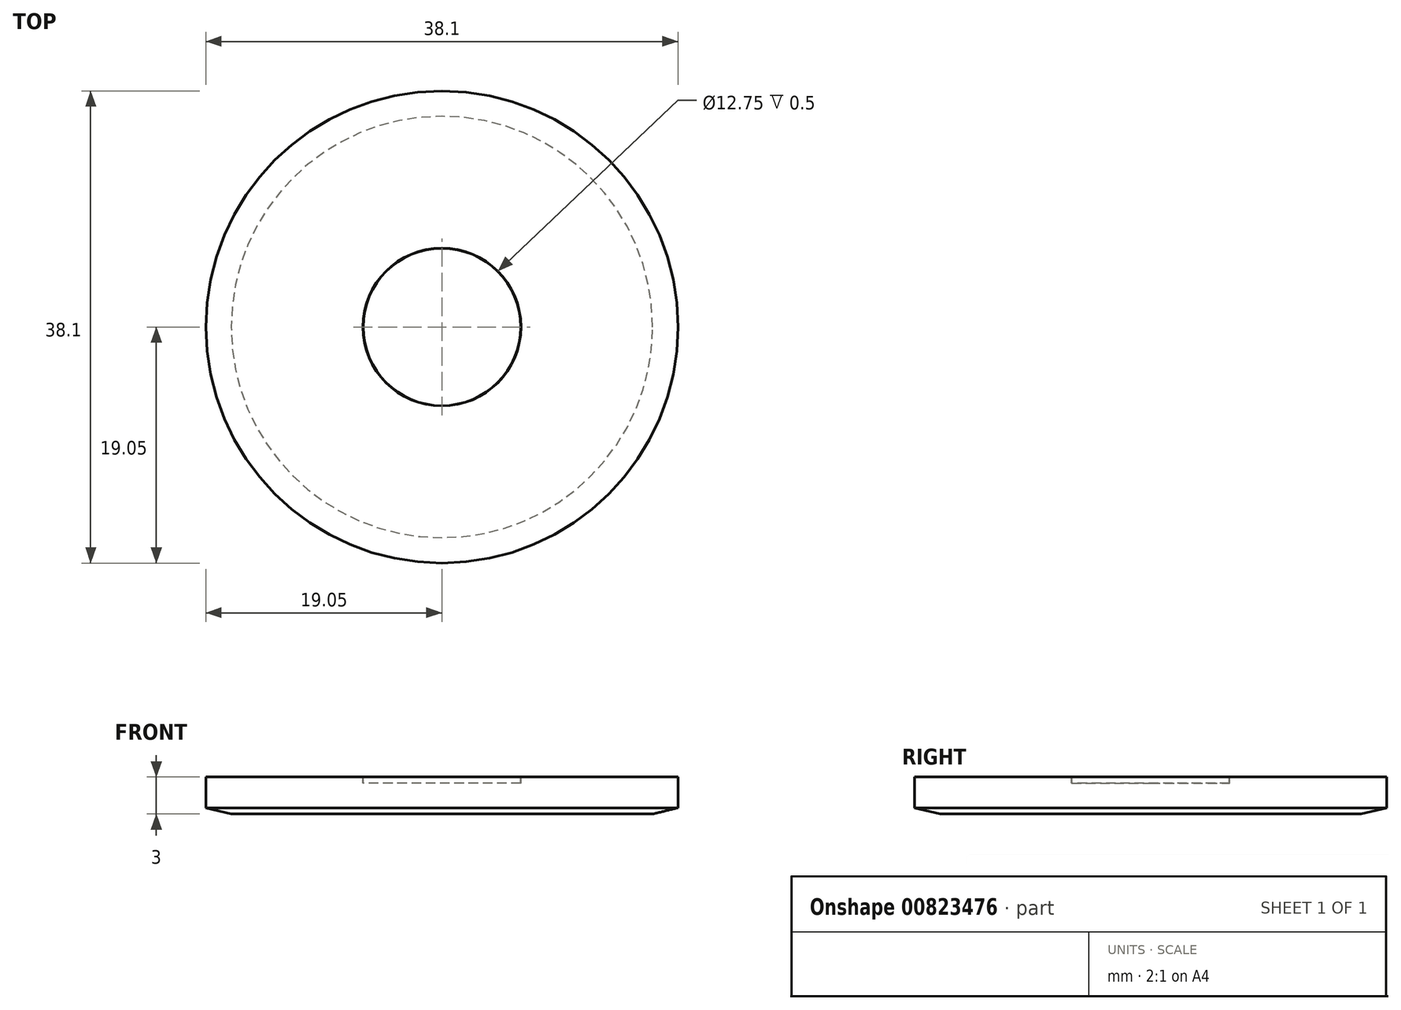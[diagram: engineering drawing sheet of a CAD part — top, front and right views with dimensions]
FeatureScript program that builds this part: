
annotation { "Feature Type Name" : "Feature", "Feature Type Description" : "" }
export const myFeature = defineFeature(function(context is Context, id is Id, definition is map)
    precondition{}
    {
        {
            var Q0;
            Q0=qCreatedBy(makeId("Top.planeOp"),FACE);
            var sketch = newSketch(context, id + "F0", { "sketchPlane" : qUnion([Q0])});
            skCircle(sketch, "E0", {"center": v(0, 0) * mm, "radius": 19.05 * mm});
            skSolve(sketch);
        }
        {
            var Q0;
            Q0=makeQuery(id+"F0.imprint","IMPRINT",FACE,{"disambiguationData":[TD([[makeQuery(id+"F0.imprint","IMPRINT",EDGE,{"derivedFrom":sQuery(id+"F0.wireOp",EDGE,"E0")}),1.0]])]});
            extrude(context, id + "F1", {"entities" : qUnion([Q0]), "depth" : 2.5 * mm, "offsetDistance" : 25 * mm});
        }
        {
            var Q0;
            Q0=makeQuery(id+"F1.opExtrude","CAP_FACE",FACE,{"disambiguationData":[OSD([sQuery(id+"F0.wireOp",EDGE,"E0")])],"isStart":false});
            var sketch = newSketch(context, id + "F2", { "sketchPlane" : qUnion([Q0])});
            skCircle(sketch, "E1", {"center": v(0, 0) * mm, "radius": 6.35 * mm});
            skCircle(sketch, "E2", {"center": v(0, 0) * mm, "radius": 6.38 * mm});
            skSolve(sketch);
        }
        {
            var Q0;
            Q0=makeQuery(id+"F2.imprint","IMPRINT",FACE,{"disambiguationData":[TD([[makeQuery(id+"F2.imprint","IMPRINT",EDGE,{"derivedFrom":sQuery(id+"F2.wireOp",EDGE,"E1")}),-1.0]])]});
            extrude(context, id + "F3", {"entities" : qUnion([Q0]), "operationType" : NewBodyOperationType.REMOVE, "oppositeDirection" : true, "depth" : .5 * mm, "offsetDistance" : 25 * mm});
        }
        {
            var Q0;
            Q0=qCreatedBy(makeId("Front.planeOp"),FACE);
            var sketch = newSketch(context, id + "F4", { "sketchPlane" : qUnion([Q0])});
            skLineSegment(sketch, "E3.0", {"start": v(-14.66, -3.4) * mm, "end": v(-8.3, -3.4) * mm});
            skArc(sketch, "E4", {"start": v(-14.66, -3.4) * mm, "mid": v(-13.73, -3.53) * mm, "end": v(-12.8, -3.65) * mm});
            skLineSegment(sketch, "E5", {"start": v(-12.8, -3.65) * mm, "end": v(-8.3, -3.65) * mm});
            skLineSegment(sketch, "E6", {"start": v(-8.3, -3.4) * mm, "end": v(-8.3, -3.65) * mm});
            skArc(sketch, "E7", {"start": v(1.27, -6.82) * mm, "mid": v(2.2, -6.95) * mm, "end": v(3.13, -7.07) * mm});
            skLineSegment(sketch, "E8", {"start": v(3.13, -7.07) * mm, "end": v(7.62, -7.07) * mm});
            skLineSegment(sketch, "E9", {"start": v(7.62, -6.82) * mm, "end": v(7.62, -7.07) * mm});
            skLineSegment(sketch, "E10", {"start": v(0, 0) * mm, "end": v(0, -0.5) * mm});
            skLineSegment(sketch, "E11", {"start": v(0, -0.5) * mm, "end": v(-17, -0.5) * mm});
            skLineSegment(sketch, "E12.0", {"start": v(-19.05, 0) * mm, "end": v(19.05, 0) * mm});
            skLineSegment(sketch, "E13", {"start": v(-17, -0.5) * mm, "end": v(-19.05, 0) * mm});
            skSolve(sketch);
        }
        {
            var Q0;
            {var subQ0=sQuery(id+"F4.wireOp",EDGE,"E10");Q0=makeQuery(id+"F4.imprint","IMPRINT",FACE,{"disambiguationData":[TD([[makeQuery(id+"F4.imprint","IMPRINT",EDGE,{"derivedFrom":subQ0}),-1.0]])]});}
            var Q1;
            Q1=sQuery(id+"F4.wireOp",EDGE,"E10");
            revolve(context, id + "F5", {"operationType" : NewBodyOperationType.ADD, "surfaceOperationType" : NewSurfaceOperationType.NEW, "entities" : qUnion([Q0]), "axis" : qUnion([Q1]), "revolveType" : RevolveType.FULL});
        }
    });
